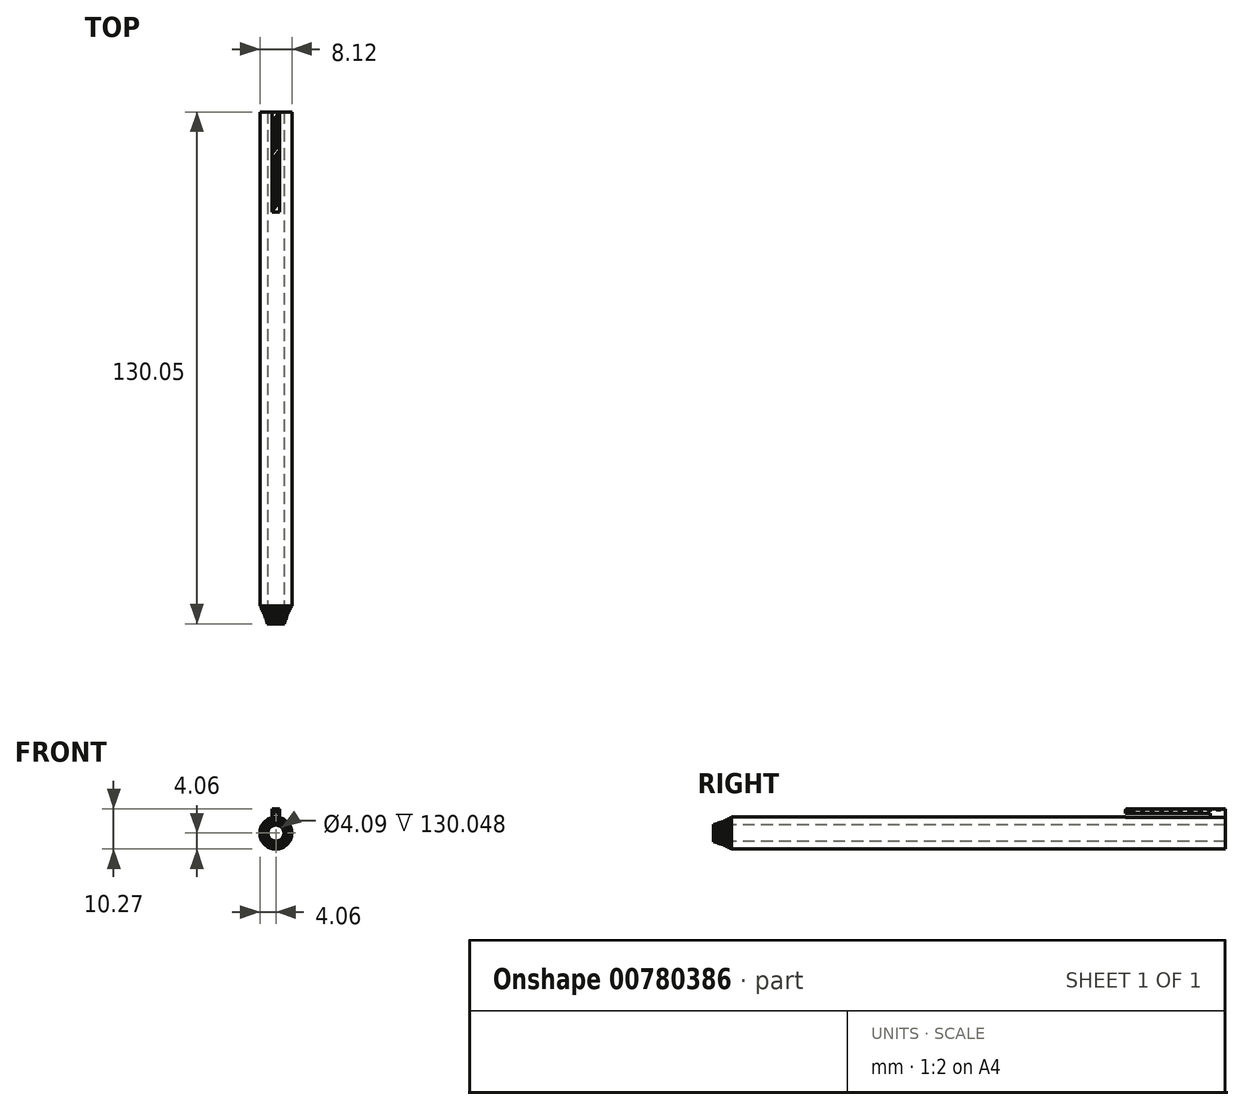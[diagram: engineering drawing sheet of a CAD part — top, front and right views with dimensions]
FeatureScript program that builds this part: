
annotation { "Feature Type Name" : "Feature", "Feature Type Description" : "" }
export const myFeature = defineFeature(function(context is Context, id is Id, definition is map)
    precondition{}
    {
        {
            var Q0;
            Q0=qCreatedBy(makeId("Front.planeOp"),FACE);
            var sketch = newSketch(context, id + "F0", { "sketchPlane" : qUnion([Q0])});
            skCircle(sketch, "E0", {"center": v(0, 0) * mm, "radius": 4.06 * mm});
            skSolve(sketch);
        }
        {
            var Q0;
            Q0=makeQuery(id+"F0.imprint","IMPRINT",FACE,{"disambiguationData":[TD([[makeQuery(id+"F0.imprint","IMPRINT",EDGE,{"derivedFrom":sQuery(id+"F0.wireOp",EDGE,"E0")}),1.0]])]});
            extrude(context, id + "F1", {"entities" : qUnion([Q0]), "depth" : 124.46 * mm, "offsetDistance" : 25.4 * mm});
        }
        {
            var Q0;
            Q0=makeQuery(id+"F1.opExtrude","CAP_FACE",FACE,{"disambiguationData":[OSD([sQuery(id+"F0.wireOp",EDGE,"E0")])],"isStart":false});
            var sketch = newSketch(context, id + "F2", { "sketchPlane" : qUnion([Q0])});
            skCircle(sketch, "E1", {"center": v(0, 0) * mm, "radius": 2.04 * mm});
            skSolve(sketch);
        }
        {
            var Q0;
            Q0=makeQuery(id+"F2.imprint","IMPRINT",FACE,{"disambiguationData":[TD([[makeQuery(id+"F2.imprint","IMPRINT",EDGE,{"derivedFrom":sQuery(id+"F2.wireOp",EDGE,"E1")}),1.0]])]});
            extrude(context, id + "F3", {"entities" : qUnion([Q0]), "operationType" : NewBodyOperationType.REMOVE, "endBound" : BoundingType.THROUGH_ALL, "oppositeDirection" : true, "depth" : 25.4 * mm, "offsetDistance" : 25.4 * mm});
        }
        {
            var Q0;
            Q0=makeQuery(id+"F1.opExtrude","CAP_FACE",FACE,{"disambiguationData":[OSD([sQuery(id+"F0.wireOp",EDGE,"E0")])],"isStart":false});
            var sketch = newSketch(context, id + "F4", { "sketchPlane" : qUnion([Q0])});
            skCircle(sketch, "E2", {"center": v(0, 0) * mm, "radius": 3.82 * mm});
            skCircle(sketch, "E3", {"center": v(0, 0) * mm, "radius": 3.58 * mm});
            skCircle(sketch, "E4", {"center": v(0, 0) * mm, "radius": 3.37 * mm});
            skCircle(sketch, "E5", {"center": v(0, 0) * mm, "radius": 3.12 * mm});
            skCircle(sketch, "E6", {"center": v(0, 0) * mm, "radius": 2.9 * mm});
            skCircle(sketch, "E7", {"center": v(0, 0) * mm, "radius": 2.73 * mm});
            skCircle(sketch, "E8", {"center": v(0, 0) * mm, "radius": 2.54 * mm});
            skCircle(sketch, "E9", {"center": v(0, 0) * mm, "radius": 2.31 * mm});
            skCircle(sketch, "E10", {"center": v(0, 0) * mm, "radius": 2.18 * mm});
            skSolve(sketch);
        }
        {
            var Q0;
            Q0=makeQuery(id+"F4.imprint","IMPRINT",FACE,{"disambiguationData":[TD([[makeQuery(id+"F4.imprint","IMPRINT",EDGE,{"derivedFrom":sQuery(id+"F4.wireOp",EDGE,"E2")}),-1.0]])]});
            extrude(context, id + "F5", {"entities" : qUnion([Q0]), "operationType" : NewBodyOperationType.ADD, "depth" : 1.02 * mm, "offsetDistance" : 25.4 * mm});
        }
        {
            var Q0;
            Q0=makeQuery(id+"F4.imprint","IMPRINT",FACE,{"disambiguationData":[TD([[makeQuery(id+"F4.imprint","IMPRINT",EDGE,{"derivedFrom":sQuery(id+"F4.wireOp",EDGE,"E2")}),1.0]])]});
            extrude(context, id + "F6", {"entities" : qUnion([Q0]), "operationType" : NewBodyOperationType.ADD, "depth" : 1.52 * mm, "offsetDistance" : 25.4 * mm});
        }
        {
            var Q0;
            Q0=makeQuery(id+"F4.imprint","IMPRINT",FACE,{"disambiguationData":[TD([[makeQuery(id+"F4.imprint","IMPRINT",EDGE,{"derivedFrom":sQuery(id+"F4.wireOp",EDGE,"E3")}),1.0]])]});
            extrude(context, id + "F7", {"entities" : qUnion([Q0]), "operationType" : NewBodyOperationType.ADD, "depth" : 2.03 * mm, "offsetDistance" : 25.4 * mm});
        }
        {
            var Q0;
            Q0=makeQuery(id+"F4.imprint","IMPRINT",FACE,{"disambiguationData":[TD([[makeQuery(id+"F4.imprint","IMPRINT",EDGE,{"derivedFrom":sQuery(id+"F4.wireOp",EDGE,"E4")}),1.0]])]});
            extrude(context, id + "F8", {"entities" : qUnion([Q0]), "operationType" : NewBodyOperationType.ADD, "depth" : 2.54 * mm, "offsetDistance" : 25.4 * mm});
        }
        {
            var Q0;
            Q0=makeQuery(id+"F4.imprint","IMPRINT",FACE,{"disambiguationData":[TD([[makeQuery(id+"F4.imprint","IMPRINT",EDGE,{"derivedFrom":sQuery(id+"F4.wireOp",EDGE,"E5")}),1.0]])]});
            extrude(context, id + "F9", {"entities" : qUnion([Q0]), "operationType" : NewBodyOperationType.ADD, "depth" : 3.05 * mm, "offsetDistance" : 25.4 * mm});
        }
        {
            var Q0;
            Q0=makeQuery(id+"F4.imprint","IMPRINT",FACE,{"disambiguationData":[TD([[makeQuery(id+"F4.imprint","IMPRINT",EDGE,{"derivedFrom":sQuery(id+"F4.wireOp",EDGE,"E6")}),1.0]])]});
            extrude(context, id + "F10", {"entities" : qUnion([Q0]), "operationType" : NewBodyOperationType.ADD, "depth" : 3.56 * mm, "offsetDistance" : 25.4 * mm});
        }
        {
            var Q0;
            Q0=makeQuery(id+"F4.imprint","IMPRINT",FACE,{"disambiguationData":[TD([[makeQuery(id+"F4.imprint","IMPRINT",EDGE,{"derivedFrom":sQuery(id+"F4.wireOp",EDGE,"E7")}),1.0]])]});
            extrude(context, id + "F11", {"entities" : qUnion([Q0]), "operationType" : NewBodyOperationType.ADD, "depth" : 4.06 * mm, "offsetDistance" : 25.4 * mm});
        }
        {
            var Q0;
            Q0=makeQuery(id+"F4.imprint","IMPRINT",FACE,{"disambiguationData":[TD([[makeQuery(id+"F4.imprint","IMPRINT",EDGE,{"derivedFrom":sQuery(id+"F4.wireOp",EDGE,"E8")}),1.0]])]});
            extrude(context, id + "F12", {"entities" : qUnion([Q0]), "operationType" : NewBodyOperationType.ADD, "depth" : 4.57 * mm, "offsetDistance" : 25.4 * mm});
        }
        {
            var Q0;
            Q0=makeQuery(id+"F4.imprint","IMPRINT",FACE,{"disambiguationData":[TD([[makeQuery(id+"F4.imprint","IMPRINT",EDGE,{"derivedFrom":sQuery(id+"F4.wireOp",EDGE,"E9")}),1.0]])]});
            extrude(context, id + "F13", {"entities" : qUnion([Q0]), "operationType" : NewBodyOperationType.ADD, "depth" : 5.08 * mm, "offsetDistance" : 25.4 * mm});
        }
        {
            var Q0;
            Q0=makeQuery(id+"F1.opExtrude","CAP_FACE",FACE,{"disambiguationData":[OSD([sQuery(id+"F0.wireOp",EDGE,"E0")])],"isStart":false});
            extrude(context, id + "F14", {"entities" : qUnion([Q0]), "operationType" : NewBodyOperationType.ADD, "depth" : 5.6 * mm, "offsetDistance" : 25.4 * mm});
        }
        {
            var Q0;
            Q0=makeQuery(id+"F1.opExtrude","CAP_FACE",FACE,{"disambiguationData":[OSD([sQuery(id+"F0.wireOp",EDGE,"E0")])],"isStart":true});
            var sketch = newSketch(context, id + "F15", { "sketchPlane" : qUnion([Q0])});
            skLineSegment(sketch, "E11.bottom", {"start": v(0.97, 5.2) * mm, "end": v(-0.97, 5.2) * mm});
            skLineSegment(sketch, "E11.left", {"start": v(0.97, 5.2) * mm, "end": v(0.97, 2.93) * mm});
            skLineSegment(sketch, "E11.right", {"start": v(-0.97, 5.2) * mm, "end": v(-0.97, 2.93) * mm});
            skPoint(sketch, "E11.middle", {"position": v(0, 4.06) * mm});
            skSolve(sketch);
        }
        {
            var Q0;
            {var subQ0=sQuery(id+"F15.wireOp",EDGE,"E11.bottom");Q0=makeQuery(id+"F15.imprint","IMPRINT",FACE,{"disambiguationData":[TD([[makeQuery(id+"F15.imprint","IMPRINT",EDGE,{"derivedFrom":subQ0}),1.0]])]});}
            extrude(context, id + "F16", {"entities" : qUnion([Q0]), "oppositeDirection" : true, "depth" : 25.4 * mm, "offsetDistance" : 25.4 * mm});
        }
        {
            var Q0;
            Q0=makeQuery(id+"F16.opExtrude","SWEPT_FACE",FACE,{"disambiguationData":[OSD([sQuery(id+"F15.wireOp",EDGE,"E11.bottom")])]});
            extrude(context, id + "F17", {"entities" : qUnion([Q0]), "operationType" : NewBodyOperationType.ADD, "depth" : 0.76 * mm, "offsetDistance" : 25.4 * mm});
        }
        {
            var Q0;
            {var subQ0=sQuery(id+"F15.wireOp",EDGE,"E11.left");Q0=makeQuery(id+"F17.boolean.opBoolean","MERGE",FACE,{"derivedFrom":[makeQuery(id+"F16.opExtrude","SWEPT_FACE",FACE,{"disambiguationData":[OSD([subQ0])]}),makeQuery(id+"F17.opExtrude","SWEPT_FACE",FACE,{"disambiguationData":[OSD([sQuery(id+"F15.wireOp",EDGE,"E11.bottom"),subQ0])]})]});}
            var sketch = newSketch(context, id + "F18", { "sketchPlane" : qUnion([Q0])});
            skLineSegment(sketch, "E12", {"start": v(25.4, 4.95) * mm, "end": v(3.87, 4.95) * mm});
            skLineSegment(sketch, "E13", {"start": v(3.87, 4.95) * mm, "end": v(3.87, 3.95) * mm});
            skSolve(sketch);
        }
        {
            var Q0;
            {var subQ0=sQuery(id+"F18.wireOp",EDGE,"E12");Q0=makeQuery(id+"F18.imprint","IMPRINT",FACE,{"disambiguationData":[TD([[makeQuery(id+"F18.imprint","IMPRINT",EDGE,{"derivedFrom":subQ0}),1.0]])]});}
            extrude(context, id + "F19", {"entities" : qUnion([Q0]), "operationType" : NewBodyOperationType.REMOVE, "oppositeDirection" : true, "depth" : 25.4 * mm, "offsetDistance" : 25.4 * mm});
        }
        {
            var Q0;
            Q0=makeQuery(id+"F17.opExtrude","CAP_FACE",FACE,{"disambiguationData":[OSD([sQuery(id+"F15.wireOp",EDGE,"E11.bottom")])],"isStart":false});
            var sketch = newSketch(context, id + "F20", { "sketchPlane" : qUnion([Q0])});
            skLineSegment(sketch, "E14", {"start": v(0.97, 0) * mm, "end": v(-0.97, -2.48) * mm});
            skLineSegment(sketch, "E15", {"start": v(0.97, -1.18) * mm, "end": v(-0.97, -3.66) * mm});
            skLineSegment(sketch, "E16", {"start": v(0.97, -2.37) * mm, "end": v(-0.97, -4.84) * mm});
            skLineSegment(sketch, "E17", {"start": v(0.97, -3.4) * mm, "end": v(-0.97, -5.87) * mm});
            skLineSegment(sketch, "E18", {"start": v(0.97, -4.58) * mm, "end": v(-0.97, -7.06) * mm});
            skLineSegment(sketch, "E19", {"start": v(-0.97, -8.25) * mm, "end": v(0.97, -5.78) * mm});
            skLineSegment(sketch, "E20", {"start": v(-0.97, -9.45) * mm, "end": v(0.97, -6.97) * mm});
            skLineSegment(sketch, "E21", {"start": v(0.97, -8.16) * mm, "end": v(-0.97, -10.64) * mm});
            skLineSegment(sketch, "E22", {"start": v(0.97, -9.72) * mm, "end": v(-0.97, -12.2) * mm});
            skLineSegment(sketch, "E23", {"start": v(-0.97, -13.39) * mm, "end": v(0.97, -10.9) * mm});
            skLineSegment(sketch, "E24", {"start": v(-0.97, -14.58) * mm, "end": v(0.97, -12.1) * mm});
            skLineSegment(sketch, "E25", {"start": v(-0.97, -15.78) * mm, "end": v(0.97, -13.3) * mm});
            skLineSegment(sketch, "E26", {"start": v(-0.97, -16.9) * mm, "end": v(0.97, -14.43) * mm});
            skLineSegment(sketch, "E27", {"start": v(-0.97, -18.1) * mm, "end": v(0.97, -15.63) * mm});
            skLineSegment(sketch, "E28", {"start": v(-0.97, -19.3) * mm, "end": v(0.97, -16.82) * mm});
            skLineSegment(sketch, "E29", {"start": v(-0.97, -20.49) * mm, "end": v(0.97, -18.02) * mm});
            skLineSegment(sketch, "E30", {"start": v(-0.97, -21.72) * mm, "end": v(0.97, -19.25) * mm});
            skLineSegment(sketch, "E31", {"start": v(-0.97, -22.91) * mm, "end": v(0.97, -20.44) * mm});
            skLineSegment(sketch, "E32", {"start": v(-0.97, -24.1) * mm, "end": v(0.97, -21.64) * mm});
            skLineSegment(sketch, "E33", {"start": v(-0.97, -25.3) * mm, "end": v(0.97, -22.84) * mm});
            skSolve(sketch);
        }
        {
            var Q0;
            {var subQ0=sQuery(id+"F20.wireOp",EDGE,"E14");Q0=makeQuery(id+"F20.imprint","IMPRINT",FACE,{"disambiguationData":[TD([[makeQuery(id+"F20.imprint","IMPRINT",EDGE,{"derivedFrom":subQ0}),1.0]])]});}
            var Q1;
            {var subQ0=sQuery(id+"F20.wireOp",EDGE,"E16");Q1=makeQuery(id+"F20.imprint","IMPRINT",FACE,{"disambiguationData":[TD([[makeQuery(id+"F20.imprint","IMPRINT",EDGE,{"derivedFrom":subQ0}),1.0]])]});}
            var Q2;
            {var subQ0=sQuery(id+"F20.wireOp",EDGE,"E18");Q2=makeQuery(id+"F20.imprint","IMPRINT",FACE,{"disambiguationData":[TD([[makeQuery(id+"F20.imprint","IMPRINT",EDGE,{"derivedFrom":subQ0}),1.0]])]});}
            var Q3;
            {var subQ0=sQuery(id+"F20.wireOp",EDGE,"E20");Q3=makeQuery(id+"F20.imprint","IMPRINT",FACE,{"disambiguationData":[TD([[makeQuery(id+"F20.imprint","IMPRINT",EDGE,{"derivedFrom":subQ0}),-1.0]])]});}
            var Q4;
            {var subQ0=sQuery(id+"F20.wireOp",EDGE,"E22");Q4=makeQuery(id+"F20.imprint","IMPRINT",FACE,{"disambiguationData":[TD([[makeQuery(id+"F20.imprint","IMPRINT",EDGE,{"derivedFrom":subQ0}),1.0]])]});}
            var Q5;
            {var subQ0=sQuery(id+"F20.wireOp",EDGE,"E24");Q5=makeQuery(id+"F20.imprint","IMPRINT",FACE,{"disambiguationData":[TD([[makeQuery(id+"F20.imprint","IMPRINT",EDGE,{"derivedFrom":subQ0}),-1.0]])]});}
            var Q6;
            {var subQ0=sQuery(id+"F20.wireOp",EDGE,"E26");Q6=makeQuery(id+"F20.imprint","IMPRINT",FACE,{"disambiguationData":[TD([[makeQuery(id+"F20.imprint","IMPRINT",EDGE,{"derivedFrom":subQ0}),-1.0]])]});}
            var Q7;
            {var subQ0=sQuery(id+"F20.wireOp",EDGE,"E28");Q7=makeQuery(id+"F20.imprint","IMPRINT",FACE,{"disambiguationData":[TD([[makeQuery(id+"F20.imprint","IMPRINT",EDGE,{"derivedFrom":subQ0}),-1.0]])]});}
            var Q8;
            {var subQ0=sQuery(id+"F20.wireOp",EDGE,"E30");Q8=makeQuery(id+"F20.imprint","IMPRINT",FACE,{"disambiguationData":[TD([[makeQuery(id+"F20.imprint","IMPRINT",EDGE,{"derivedFrom":subQ0}),-1.0]])]});}
            var Q9;
            {var subQ0=sQuery(id+"F20.wireOp",EDGE,"E32");Q9=makeQuery(id+"F20.imprint","IMPRINT",FACE,{"disambiguationData":[TD([[makeQuery(id+"F20.imprint","IMPRINT",EDGE,{"derivedFrom":subQ0}),-1.0]])]});}
            extrude(context, id + "F21", {"entities" : qUnion([Q0, Q1, Q2, Q3, Q4, Q5, Q6, Q7, Q8, Q9]), "operationType" : NewBodyOperationType.ADD, "depth" : 0.25 * mm, "offsetDistance" : 25.4 * mm});
        }
    });
